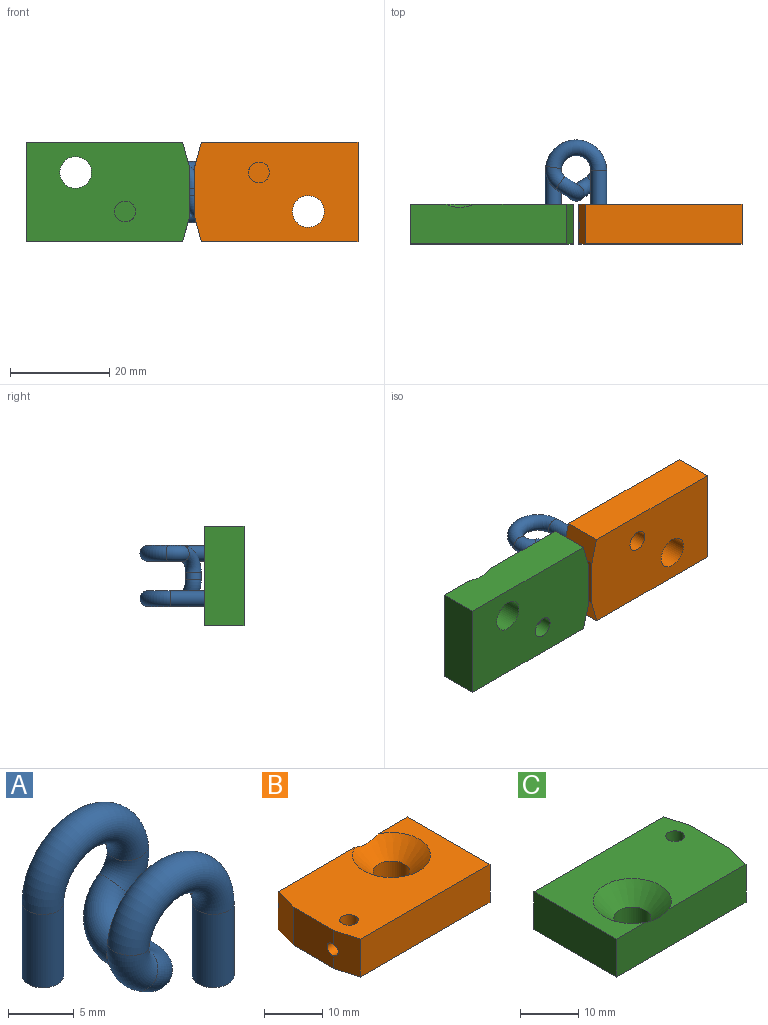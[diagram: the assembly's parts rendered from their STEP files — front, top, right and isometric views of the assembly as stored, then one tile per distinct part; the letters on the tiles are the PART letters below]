
ASSEMBLY  parts=3 mates=8
PART A: 20 faces, bbox 13.4x13.2x13.5 mm
  f0: cylinder r=1.23mm len=6.82mm, axis (0,0,1), area 52.8mm2, adj f1,f9
  f1: torus R=4.59mm, axis (0,1,0), area 106.9mm2, adj f0,f2
  f2: torus R=3.17mm, axis (0,1,0), area 27.3mm2, adj f1,f3
  f3: torus R=3.83mm, axis (-0.56,0,0.83), area 46.6mm2, adj f2,f4
  f4: cylinder r=1.23mm len=2.46mm, axis (0,-1,0), area 11.5mm2, adj f3,f5
  f5: torus R=3.83mm, axis (-0.56,0,-0.83), area 46.6mm2, adj f4,f6
  f6: torus R=3.17mm, axis (0,1,0), area 27.3mm2, adj f5,f7
  f7: torus R=4.59mm, axis (0,1,0), area 106.9mm2, adj f6,f8
  f8: cylinder r=1.23mm len=6.82mm, axis (0,0,-1), area 52.8mm2, adj f7,f10
  f9: plane 3.18x3.18mm, normal (0,0,-1), area 3.1mm2, adj f0,f11
  f10: plane 3.18x3.18mm, normal (0,0,-1), area 3.1mm2, adj f8,f19
  f11: cylinder r=1.59mm len=6.82mm, axis (0,0,1), area 68.1mm2, adj f9,f12
  f12: torus R=4.59mm, axis (0,1,0), area 137.7mm2, adj f11,f13
  f13: torus R=3.17mm, axis (0,1,0), area 35.1mm2, adj f12,f14
  f14: torus R=3.83mm, axis (-0.56,0,0.83), area 60mm2, adj f13,f15
  f15: cylinder r=1.59mm len=3.18mm, axis (0,-1,0), area 14.8mm2, adj f14,f16
  f16: torus R=3.83mm, axis (-0.56,0,-0.83), area 60mm2, adj f15,f17
  f17: torus R=3.17mm, axis (0,1,0), area 35.1mm2, adj f16,f18
  f18: torus R=4.59mm, axis (0,1,0), area 137.7mm2, adj f17,f19
  f19: cylinder r=1.59mm len=6.82mm, axis (0,0,-1), area 68.1mm2, adj f10,f18
PART B: 20 faces, bbox 33x20.7x8 mm
  f0: cylinder r=1.24mm len=12.05mm, axis (-1,0,0), area 74.5mm2, adj f1,f6,f11,f13,f14,f15
  f1: plane 9.9x8mm, normal (-1,0,0), area 75.8mm2, adj f0,f3,f5,f6,f8
  f2: plane 31.62x8.01mm, normal (0,1,0), area 238.4mm2, adj f3,f4,f5,f8,f10,f17,f19
  f3: plane 33x20.07mm, normal (0,0,1), area 507.6mm2, adj f1,f2,f4,f5,f6,f7,f10,f13
  f4: plane 20.07x8mm, normal (1,0,0), area 160.5mm2, adj f2,f3,f7,f8
  f5: plane 8x5.09mm, normal (-0.97,0.26,0), area 42.2mm2, adj f1,f2,f3,f8
  f6: plane 8x5.09mm, normal (-0.97,-0.26,0), area 40.6mm2, adj f0,f1,f3,f7,f8
  f7: plane 31.62x8mm, normal (0,-1,0), area 253mm2, adj f3,f4,f6,f8
  f8: plane 33x20.07mm, normal (0,0,-1), area 609mm2, adj f1,f2,f4,f5,f6,f7,f9,f11
  f9: cylinder r=3.2mm len=6.4mm, axis (0,0,1), area 90.1mm2, adj f8,f10
  f10: cone r=3.2mm half-angle=45deg, axis (0,0,1), area 151.8mm2, adj f2,f3,f9
  f11: cylinder r=2.11mm len=5.59mm, axis (0,0,-1), area 68.6mm2, adj f0,f8,f12
  f12: plane 4.22x4.22mm, normal (0,0,-1), area 14mm2, adj f11
  f13: cylinder r=1.6mm len=4.76mm, axis (0,0,1), area 39.4mm2, adj f0,f3,f14,f15
  f14: plane 2.31x0.49mm, normal (0,0,1), area 0.8mm2, adj f0,f13
  f15: plane 2.31x0.49mm, normal (0,0,1), area 0.8mm2, adj f0,f13
  f16: cone r=0mm half-angle=59deg, axis (0,1,0), area 7.2mm2, adj f17
  f17: cylinder r=1.4mm len=7.62mm, axis (0,1,0), area 67mm2, adj f2,f16
  f18: cone r=0mm half-angle=59deg, axis (0,1,0), area 7.2mm2, adj f19
  f19: cylinder r=1.4mm len=7.62mm, axis (0,1,0), area 67mm2, adj f2,f18
PART C: 20 faces, bbox 33.1x20.8x8.1 mm
  f0: plane 2.31x0.49mm, normal (0,0,1), area 0.8mm2, adj f13,f15
  f1: plane 31.62x8.01mm, normal (0,-1,0), area 250.7mm2, adj f2,f4,f5,f8,f10
  f2: plane 33.02x20.07mm, normal (0,0,1), area 507.9mm2, adj f1,f3,f4,f5,f6,f7,f10,f13
  f3: plane 31.62x8mm, normal (0,1,0), area 240.7mm2, adj f2,f4,f7,f8,f17,f19
  f4: plane 20.07x8mm, normal (-1,0,0), area 160.5mm2, adj f1,f2,f3,f8
  f5: plane 8x5.08mm, normal (0.96,-0.27,0), area 42.2mm2, adj f1,f2,f6,f8
  f6: plane 9.91x8mm, normal (1,0,0), area 75.9mm2, adj f2,f5,f7,f8,f15
  f7: plane 8.11x5.19mm, normal (0.96,0.27,0), area 40.6mm2, adj f2,f3,f6,f8,f15
  f8: plane 33.02x20.07mm, normal (0,0,-1), area 609.3mm2, adj f1,f3,f4,f5,f6,f7,f9,f11
  f9: cylinder r=3.2mm len=6.4mm, axis (0,0,1), area 90.1mm2, adj f8,f10
  f10: cone r=3.2mm half-angle=45deg, axis (0,0,1), area 151.8mm2, adj f1,f2,f9
  f11: cylinder r=2.11mm len=5.59mm, axis (0,0,-1), area 68.5mm2, adj f8,f12,f15
  f12: plane 4.22x4.22mm, normal (0,0,-1), area 14mm2, adj f11
  f13: cylinder r=1.6mm len=4.76mm, axis (0,0,1), area 39.5mm2, adj f0,f2,f14,f15
  f14: plane 2.31x0.49mm, normal (0,0,1), area 0.8mm2, adj f13,f15
  f15: cylinder r=1.24mm len=12.07mm, axis (1,0,0), area 74.8mm2, adj f0,f6,f7,f11,f13,f14
  f16: cone r=0mm half-angle=59deg, axis (0,1,0), area 7.2mm2, adj f17
  f17: cylinder r=1.4mm len=7.62mm, axis (0,1,0), area 67mm2, adj f3,f16
  f18: cone r=0mm half-angle=59deg, axis (0,1,0), area 7.2mm2, adj f19
  f19: cylinder r=1.4mm len=7.62mm, axis (0,1,0), area 67mm2, adj f3,f18
PLACE A rot(axis=(-1,0,0),90deg) t=(-33.5,0,-10.03)mm
PLACE B rot(axis=(-1,0,0),90deg) t=(-33.5,0,-10.03)mm
PLACE C rot(axis=(-1,0,0),90deg) t=(-33.5,0,-10.03)mm
MATE cylindrical A.f8 <-> B.f13  axis (0,-1,0) through (-28.91,11.41,-5.46)mm
MATE cylindrical C.f13 <-> A.f0  axis (0,1,0) through (-38.09,8,-14.61)mm
MATE parallel B.f4 <-> C.f4  axis (1,0,0) through (0,4,-10.03)mm
MATE parallel C.f4 <-> B.f4  axis (-1,0,0) through (-67.02,4,-10.03)mm
MATE planar B.f3 <-> A.f8  axis (0,1,0) through (-17.86,8,-9.05)mm
MATE parallel C.f2 <-> B.f3  axis (0,1,0) through (-49.15,8,-11.01)mm
MATE planar C.f3 <-> B.f2  axis (0,0,-1) through (-50.89,4,-20.07)mm
MATE planar C.f8 <-> B.f8  axis (0,-1,0) through (-50.43,0,-10.15)mm
